# Revit family: P300320-163
name_source: partatom
category: Lighting Fixtures
units: mm (PartAtom-declared; Revit-internal decimal feet)

## family parameters
Cut with Voids When Loaded = No
Host = Face
Light Source = Yes
OmniClass Number = 23.80.70.11.14.17
OmniClass Title = Direct/Indirect
Part Type = Normal
Room Calculation Point = No
Round Connector Dimension = Use Diameter
Shared = Yes

## types (1)
- P300320-163
    Apparent Load = 60 VA
    Color Filter = 16777215
    Connector Description = Lighting Connector
    Default Elevation = 48 "
    Description = Enjoy delightful charming details with the Aiken Collection 1-Light Brushed Nickel Clear Glass Vintage Bath Vanity Light. The beveled backplate, elegantly curved arm, and vintage light base are coated in a beautiful brushed nickel finish. A light source glows from inside a clear glass shade reminiscent of vintage apothecary bottles.
    Dimming Lamp Color Temperature Shift = <None>
    Features = Application: Enjoy delightful charming details with the Aiken Collection 1-Light Brushed Nickel Clear Glass Vintage Bath Vanity Light ideal for any entryway, hallway, foyer, bedroom, sitting room, living room, or bathroom.
Styles: Perfect for farmhouse, coastal, and vintage electric style settings.
Finish: The beveled backplate, elegantly curved arm, and vintage light base are coated in a beautiful brushed nickel finish.
Materials: Constructed from steel to ensure a long product lifespan. Mount the light fixture facing up or down.
Glass/Shade: A light source glows from inside a clear glass shade reminiscent of vintage apothecary bottles.
Bulbs: For ideal illumination, use 1 medium base bulb that is sold separately (60w max - LED/CFL/incandescent). Compatible with dimmable bulbs.
Dimensions: Measures 4-1/2-inch width by 9-7/8-inch height by 7-inch depth.
Certifications: cULus Damp Location Listed.
Pairs With: Pairs with a variety of Progress Lighting fixtures.
Warranty: Our 1-Year Limited Warranty guarantees your complete satisfaction with your purchase and includes professional after-sales customer service support.
    Fixture distribution = Direct
    Glass = Paint - Hubbell - White Texture
    Gold = Hubbell - Gold
    Height = 6.5 "
    Housing Material = Paint - Hubbell - Vintage Bronze
    Lamp = LED
    Load Classification = Lighting
    Manufacturer = Progress Lighting
    Model = P300320-163
    Photometric Web File = generic.ies
    Power Factor = 1
    Product Documentation Link = https://hubbellcdn.com
    Product Link = https://www.hubbell.com
    Support = Paint - Hubbell - Light Silver
    Tilt Angle = -90.00°
    URL = https://www.hubbell.com
    Voltage = 120 V
    Warranty = 1 year Warranty
    Wattage Comments = 60W
    Watts = 60 W
    Width = 4.5 "

## geometry (parser evidence)
native form markers: Sweep x2
no freeform markers — native parametric forms only
